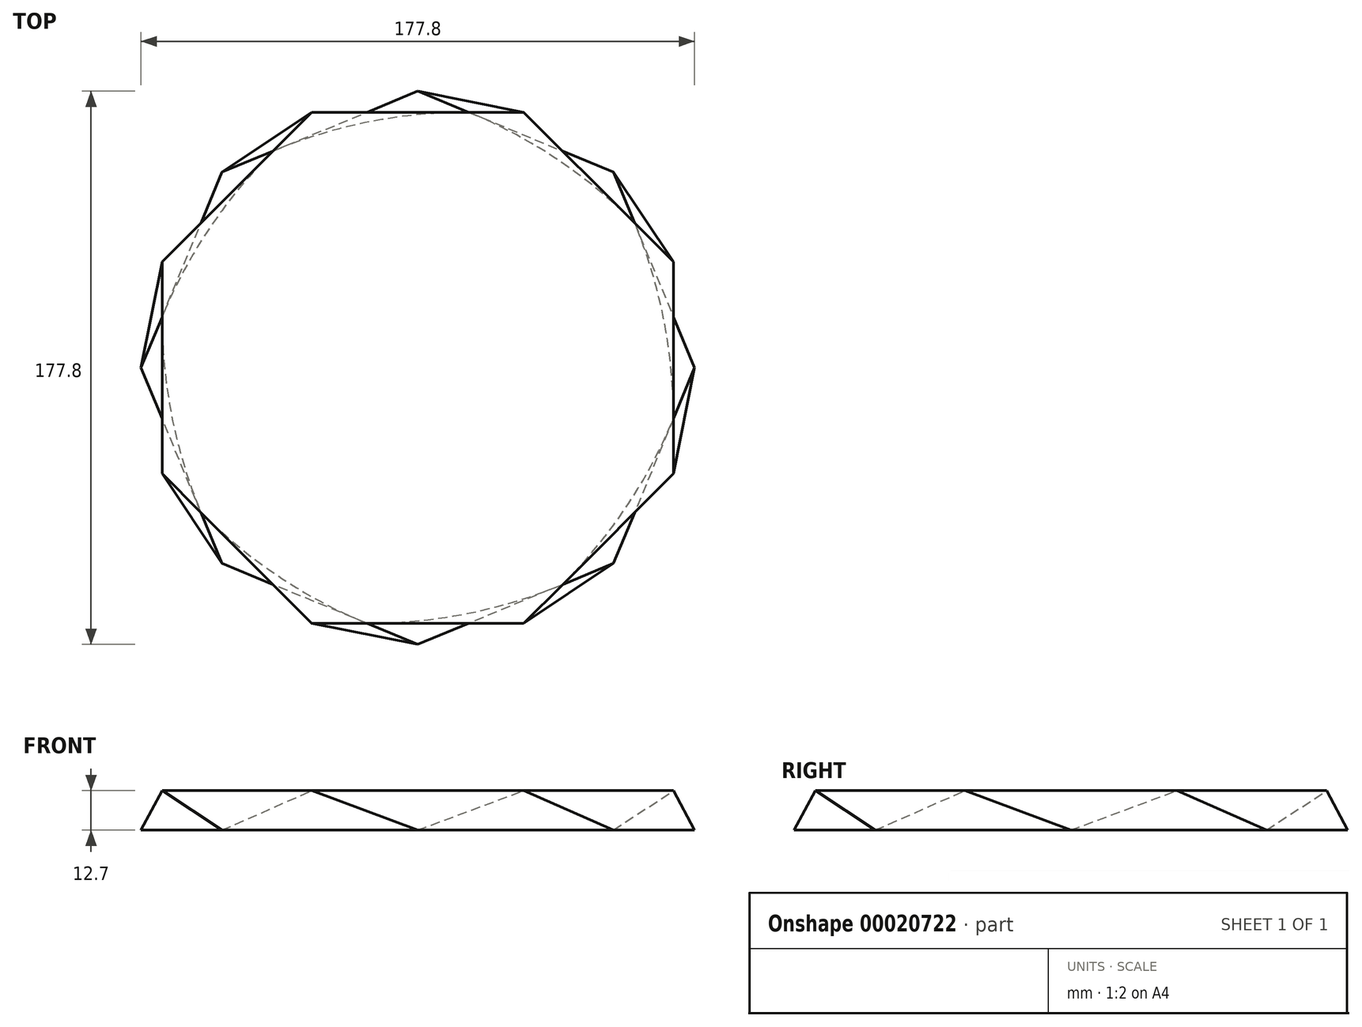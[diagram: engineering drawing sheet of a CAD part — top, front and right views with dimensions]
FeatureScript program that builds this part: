
annotation { "Feature Type Name" : "Feature", "Feature Type Description" : "" }
export const myFeature = defineFeature(function(context is Context, id is Id, definition is map)
    precondition{}
    {
        {
            var Q0;
            Q0=qCreatedBy(makeId("Top.planeOp"),FACE);
            var sketch = newSketch(context, id + "F0", { "sketchPlane" : qUnion([Q0])});
            skLineSegment(sketch, "E0.rect.bottom", {"start": v(88.9, -88.9) * mm, "end": v(-88.9, -88.9) * mm, "construction": true});
            skLineSegment(sketch, "E0.rect.top", {"start": v(88.9, 88.9) * mm, "end": v(-88.9, 88.9) * mm, "construction": true});
            skLineSegment(sketch, "E0.rect.left", {"start": v(88.9, -88.9) * mm, "end": v(88.9, 88.9) * mm, "construction": true});
            skLineSegment(sketch, "E0.rect.right", {"start": v(-88.9, -88.9) * mm, "end": v(-88.9, 88.9) * mm, "construction": true});
            skPoint(sketch, "E0.rect.middle", {"position": v(0, 0) * mm});
            skCircle(sketch, "E1.cCircle", {"center": v(0, 0) * mm, "radius": 88.9 * mm, "construction": true});
            skLineSegment(sketch, "E1.0", {"start": v(0, 88.9) * mm, "end": v(62.86, 62.86) * mm});
            skLineSegment(sketch, "E1.1", {"start": v(62.86, 62.86) * mm, "end": v(88.9, 0) * mm});
            skLineSegment(sketch, "E1.2", {"start": v(88.9, 0) * mm, "end": v(62.86, -62.86) * mm});
            skLineSegment(sketch, "E1.3", {"start": v(62.86, -62.86) * mm, "end": v(0, -88.9) * mm});
            skLineSegment(sketch, "E1.4", {"start": v(0, -88.9) * mm, "end": v(-62.86, -62.86) * mm});
            skLineSegment(sketch, "E1.5", {"start": v(-62.86, -62.86) * mm, "end": v(-88.9, 0) * mm});
            skLineSegment(sketch, "E1.6", {"start": v(-88.9, 0) * mm, "end": v(-62.86, 62.86) * mm});
            skLineSegment(sketch, "E1.7", {"start": v(-62.86, 62.86) * mm, "end": v(0, 88.9) * mm});
            skSolve(sketch);
        }
        {
            var Q0;
            Q0=qCreatedBy(makeId("Top.planeOp"),FACE);
            cPlane(context, id + "F1", {"entities" : qUnion([Q0]), "cplaneType" : CPlaneType.OFFSET, "offset" : 12.7 * mm, "width" : 152.4 * mm, "height" : 152.4 * mm});
        }
        {
            var Q0;
            Q0=qCreatedBy(id+"F1.planeOp",FACE);
            var sketch = newSketch(context, id + "F2", { "sketchPlane" : qUnion([Q0])});
            skCircle(sketch, "E2.cCircle", {"center": v(0, 0) * mm, "radius": 88.9 * mm, "construction": true});
            skLineSegment(sketch, "E2.0", {"start": v(-34.02, -82.13) * mm, "end": v(-82.13, -34.02) * mm});
            skLineSegment(sketch, "E2.1", {"start": v(-82.13, -34.02) * mm, "end": v(-82.13, 34.02) * mm});
            skLineSegment(sketch, "E2.2", {"start": v(-82.13, 34.02) * mm, "end": v(-34.02, 82.13) * mm});
            skLineSegment(sketch, "E2.3", {"start": v(-34.02, 82.13) * mm, "end": v(34.02, 82.13) * mm});
            skLineSegment(sketch, "E2.4", {"start": v(34.02, 82.13) * mm, "end": v(82.13, 34.02) * mm});
            skLineSegment(sketch, "E2.5", {"start": v(82.13, 34.02) * mm, "end": v(82.13, -34.02) * mm});
            skLineSegment(sketch, "E2.6", {"start": v(82.13, -34.02) * mm, "end": v(34.02, -82.13) * mm});
            skLineSegment(sketch, "E2.7", {"start": v(34.02, -82.13) * mm, "end": v(-34.02, -82.13) * mm});
            skSolve(sketch);
        }
        {
            var Q0;
            Q0=makeQuery(id+"F0.imprint","IMPRINT",FACE,{"disambiguationData":[TD([[makeQuery(id+"F0.imprint","IMPRINT",EDGE,{"derivedFrom":sQuery(id+"F0.wireOp",EDGE,"E1.0")}),-1.0]])]});
            var Q1;
            Q1=makeQuery(id+"F2.imprint","IMPRINT",FACE,{"disambiguationData":[TD([[makeQuery(id+"F2.imprint","IMPRINT",EDGE,{"derivedFrom":sQuery(id+"F2.wireOp",EDGE,"E2.0")}),-1.0]])]});
            loft(context, id + "F3", {"sheetProfilesArray" : [{ "sheetProfileEntities" : qUnion([Q0]) }, { "sheetProfileEntities" : qUnion([Q1]) }]});
        }
    });
